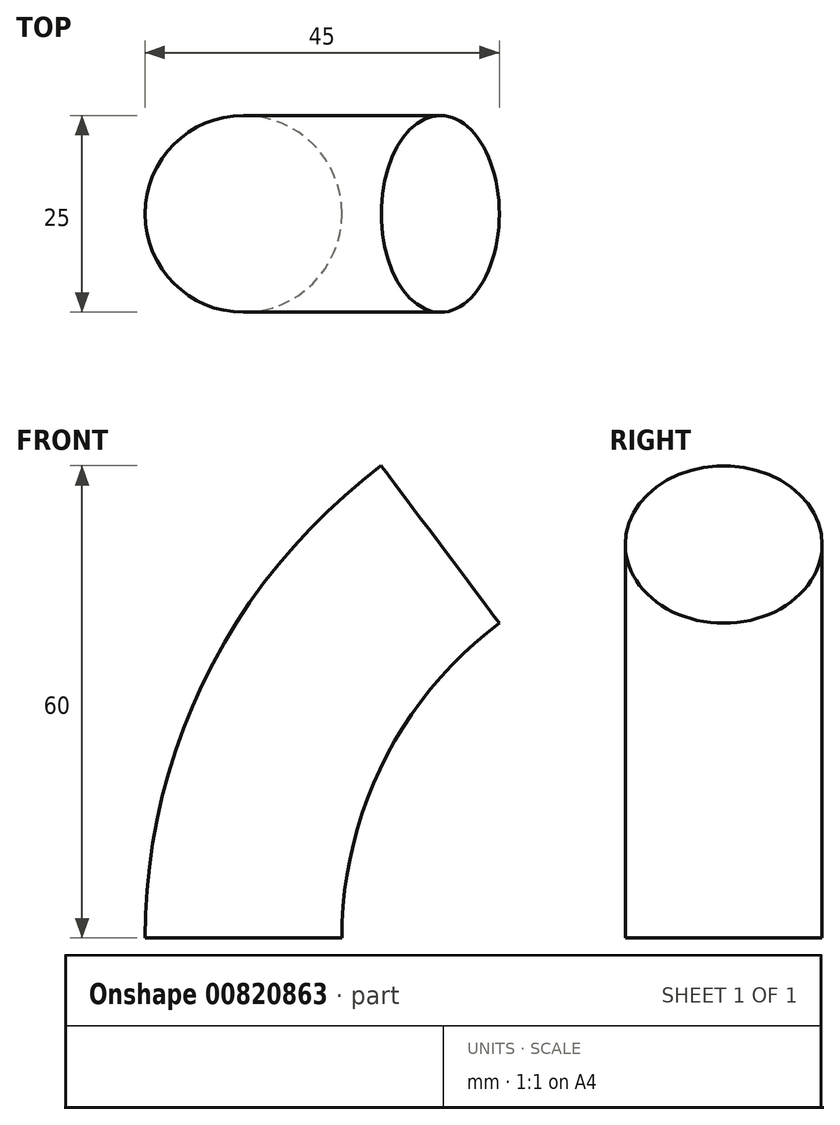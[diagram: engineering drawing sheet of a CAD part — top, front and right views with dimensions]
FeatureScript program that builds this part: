
annotation { "Feature Type Name" : "Feature", "Feature Type Description" : "" }
export const myFeature = defineFeature(function(context is Context, id is Id, definition is map)
    precondition{}
    {
        {
            var Q0;
            Q0=qCreatedBy(makeId("Top.planeOp"),FACE);
            var sketch = newSketch(context, id + "F0", { "sketchPlane" : qUnion([Q0])});
            skCircle(sketch, "E0", {"center": v(0, 0) * mm, "radius": 12.5 * mm});
            skCircle(sketch, "E1", {"center": v(0, 0) * mm, "radius": 8.5 * mm, "construction": true});
            skCircle(sketch, "E2", {"center": v(-2.5, -8.12) * mm, "radius": 2.25 * mm, "construction": true});
            skCircle(sketch, "E3", {"center": v(2.5, -8.12) * mm, "radius": 2.25 * mm, "construction": true});
            skCircle(sketch, "E4", {"center": v(8.29, 1.9) * mm, "radius": 2.25 * mm, "construction": true});
            skCircle(sketch, "E5", {"center": v(5.79, 6.23) * mm, "radius": 2.25 * mm, "construction": true});
            skCircle(sketch, "E6", {"center": v(-5.79, 6.23) * mm, "radius": 2.25 * mm, "construction": true});
            skCircle(sketch, "E7", {"center": v(-8.29, 1.9) * mm, "radius": 2.25 * mm, "construction": true});
            skLineSegment(sketch, "E8", {"start": v(0, 0) * mm, "end": v(7.36, 4.25) * mm, "construction": true});
            skLineSegment(sketch, "E9", {"start": v(0, 0) * mm, "end": v(-7.36, 4.25) * mm, "construction": true});
            skLineSegment(sketch, "E10", {"start": v(0, 0) * mm, "end": v(0, -8.5) * mm, "construction": true});
            skCircle(sketch, "E11", {"center": v(0, 0) * mm, "radius": 4.45 * mm, "construction": true});
            skSolve(sketch);
        }
        {
            var Q0;
            Q0=qCreatedBy(makeId("Front.planeOp"),FACE);
            var sketch = newSketch(context, id + "F1", { "sketchPlane" : qUnion([Q0])});
            skArc(sketch, "E12", {"start": v(25, 50) * mm, "mid": v(6.6, 27.95) * mm, "end": v(0, 0) * mm});
            skLineSegment(sketch, "E13", {"start": v(0, 0) * mm, "end": v(0, 25) * mm, "construction": true});
            skSolve(sketch);
        }
        {
            var Q0;
            Q0=makeQuery(id+"F0.imprint","IMPRINT",FACE,{"disambiguationData":[TD([[makeQuery(id+"F0.imprint","IMPRINT",EDGE,{"derivedFrom":sQuery(id+"F0.wireOp",EDGE,"E0")}),1.0]])]});
            var Q1;
            Q1=sQuery(id+"F1.wireOp",EDGE,"E12");
            sweep(context, id + "F2", {"profiles" : qUnion([Q0]), "path" : qUnion([Q1])});
        }
    });
